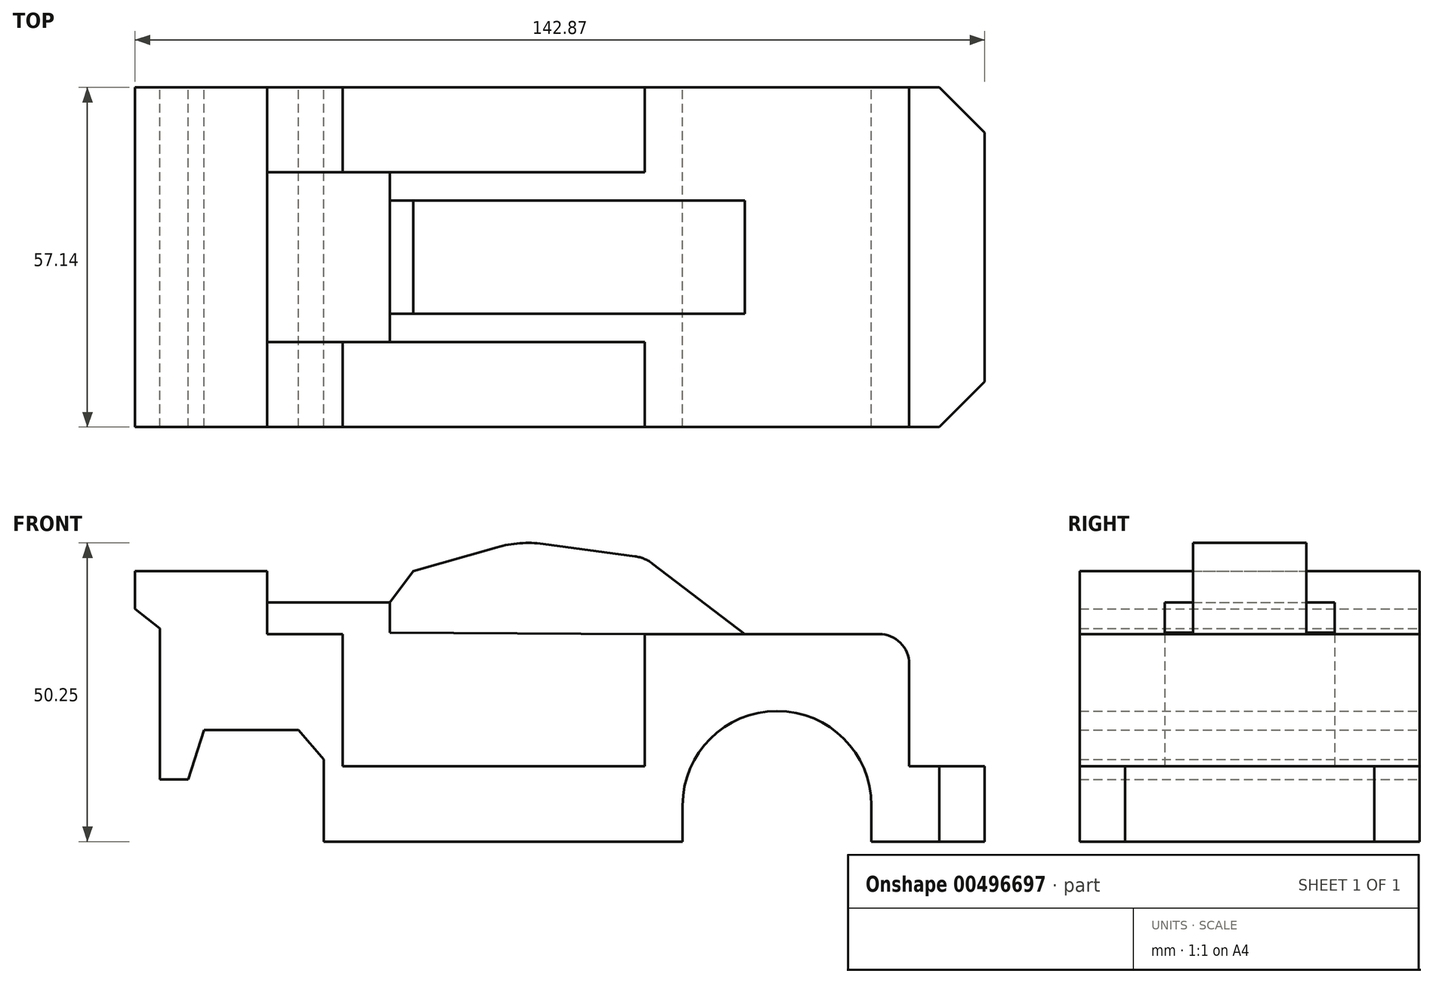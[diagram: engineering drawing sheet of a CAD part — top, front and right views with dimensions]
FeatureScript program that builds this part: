
annotation { "Feature Type Name" : "Feature", "Feature Type Description" : "" }
export const myFeature = defineFeature(function(context is Context, id is Id, definition is map)
    precondition{}
    {
        {
            var Q0;
            Q0=qCreatedBy(makeId("Front.planeOp"),FACE);
            var sketch = newSketch(context, id + "F0", { "sketchPlane" : qUnion([Q0])});
            skLineSegment(sketch, "E0", {"start": v(-32.86, -25.44) * mm, "end": v(27.46, -25.44) * mm});
            skLineSegment(sketch, "E1", {"start": v(-32.86, -25.44) * mm, "end": v(-32.86, -11.64) * mm});
            skLineSegment(sketch, "E2", {"start": v(-55.7, -14.97) * mm, "end": v(-60.47, -14.97) * mm});
            skLineSegment(sketch, "E3", {"start": v(-60.47, -14.97) * mm, "end": v(-60.47, 10.43) * mm});
            skLineSegment(sketch, "E4", {"start": v(-60.47, 10.43) * mm, "end": v(-64.61, 13.74) * mm});
            skLineSegment(sketch, "E5", {"start": v(-64.61, 13.74) * mm, "end": v(-64.61, 20.1) * mm});
            skLineSegment(sketch, "E6", {"start": v(-64.61, 20.1) * mm, "end": v(-42.39, 20.1) * mm});
            skLineSegment(sketch, "E7", {"start": v(-42.39, 20.1) * mm, "end": v(-42.39, 9.48) * mm});
            skLineSegment(sketch, "E8", {"start": v(-42.39, 9.48) * mm, "end": v(-29.69, 9.48) * mm});
            skLineSegment(sketch, "E9", {"start": v(-29.69, 9.48) * mm, "end": v(-29.69, -12.74) * mm});
            skLineSegment(sketch, "E10", {"start": v(-29.69, -12.74) * mm, "end": v(21.11, -12.74) * mm});
            skLineSegment(sketch, "E11", {"start": v(21.11, -12.74) * mm, "end": v(21.11, 9.48) * mm});
            skLineSegment(sketch, "E12", {"start": v(21.11, 9.48) * mm, "end": v(65.56, 9.48) * mm});
            skLineSegment(sketch, "E13", {"start": v(65.56, 9.48) * mm, "end": v(65.56, -12.74) * mm});
            skLineSegment(sketch, "E14", {"start": v(65.56, -12.74) * mm, "end": v(78.26, -12.74) * mm});
            skLineSegment(sketch, "E15", {"start": v(78.26, -12.74) * mm, "end": v(78.26, -18.23) * mm});
            skLineSegment(sketch, "E16", {"start": v(78.26, -18.23) * mm, "end": v(78.26, -25.44) * mm});
            skLineSegment(sketch, "E17", {"start": v(78.26, -25.44) * mm, "end": v(59.21, -25.44) * mm});
            skLineSegment(sketch, "E18", {"start": v(-42.39, 14.79) * mm, "end": v(-21.76, 14.79) * mm});
            skLineSegment(sketch, "E19", {"start": v(-21.76, 14.79) * mm, "end": v(-21.76, 9.7) * mm});
            skLineSegment(sketch, "E20", {"start": v(-21.76, 9.7) * mm, "end": v(-29.69, 9.48) * mm});
            skLineSegment(sketch, "E21", {"start": v(21.11, 9.48) * mm, "end": v(-21.76, 9.7) * mm});
            skLineSegment(sketch, "E22", {"start": v(-21.76, 14.79) * mm, "end": v(-17.81, 20.1) * mm});
            skLineSegment(sketch, "E23", {"start": v(-17.81, 20.1) * mm, "end": v(-3.76, 24.08) * mm});
            skLineSegment(sketch, "E24", {"start": v(3.99, 24.64) * mm, "end": v(19.44, 22.55) * mm});
            skLineSegment(sketch, "E25", {"start": v(22.45, 21.3) * mm, "end": v(37.9, 9.48) * mm});
            skPoint(sketch, "E26.visualSharp", {"position": v(21.11, 22.33) * mm});
            skArc(sketch, "E26.filletArc", {"start": v(22.45, 21.3) * mm, "mid": v(21.03, 22.12) * mm, "end": v(19.44, 22.55) * mm});
            skPoint(sketch, "E27.visualSharp", {"position": v(0.06, 25.17) * mm});
            skArc(sketch, "E27.filletArc", {"start": v(3.99, 24.64) * mm, "mid": v(0.09, 24.76) * mm, "end": v(-3.76, 24.08) * mm});
            skLineSegment(sketch, "E28", {"start": v(-55.7, -14.97) * mm, "end": v(-53.01, -6.67) * mm});
            skLineSegment(sketch, "E29", {"start": v(-53.01, -6.67) * mm, "end": v(-37.14, -6.67) * mm});
            skLineSegment(sketch, "E30", {"start": v(-37.14, -6.67) * mm, "end": v(-32.86, -11.64) * mm});
            skLineSegment(sketch, "E31", {"start": v(27.46, -25.44) * mm, "end": v(27.46, -19.35) * mm});
            skLineSegment(sketch, "E32", {"start": v(59.21, -25.44) * mm, "end": v(59.21, -19.35) * mm});
            skArc(sketch, "E33", {"start": v(59.21, -19.35) * mm, "mid": v(43.34, -3.47) * mm, "end": v(27.46, -19.35) * mm});
            skSolve(sketch);
        }
        {
            var Q0;
            Q0=makeQuery(id+"F0.imprint","IMPRINT",FACE,{"disambiguationData":[TD([[makeQuery(id+"F0.imprint","IMPRINT",EDGE,{"derivedFrom":sQuery(id+"F0.wireOp",EDGE,"E0")}),1.0]])]});
            extrude(context, id + "F1", {"entities" : qUnion([Q0]), "endBound" : BoundingType.SYMMETRIC, "depth" : 57.15 * mm});
        }
        {
            var Q0;
            Q0=makeQuery(id+"F0.imprint","IMPRINT",FACE,{"disambiguationData":[TD([[makeQuery(id+"F0.imprint","IMPRINT",EDGE,{"derivedFrom":sQuery(id+"F0.wireOp",EDGE,"E9")}),1.0]])]});
            extrude(context, id + "F2", {"entities" : qUnion([Q0]), "operationType" : NewBodyOperationType.ADD, "endBound" : BoundingType.SYMMETRIC, "depth" : 28.57 * mm});
        }
        {
            var Q0;
            {var subQ1=sQuery(id+"F0.wireOp",EDGE,"E8");Q0=makeQuery(id+"F0.imprint","IMPRINT",FACE,{"disambiguationData":[TD([[makeQuery(id+"F0.imprint","IMPRINT",EDGE,{"derivedFrom":subQ1}),1.0]])]});}
            extrude(context, id + "F3", {"entities" : qUnion([Q0]), "operationType" : NewBodyOperationType.ADD, "endBound" : BoundingType.SYMMETRIC, "depth" : 28.57 * mm});
        }
        {
            var Q0;
            Q0=makeQuery(id+"F1.opExtrude","SWEPT_EDGE",EDGE,{"disambiguationData":[OSD([sQuery(id+"F0.wireOp",EDGE,"E12"),sQuery(id+"F0.wireOp",EDGE,"E13")])]});
            fillet(context, id + "F4", {"entities" : qUnion([Q0]), "radius" : 5.08 * mm, "tangentPropagation" : true, "allowEdgeOverflow" : false});
        }
        {
            var Q0;
            Q0=makeQuery(id+"F0.imprint","IMPRINT",FACE,{"disambiguationData":[TD([[makeQuery(id+"F0.imprint","IMPRINT",EDGE,{"derivedFrom":sQuery(id+"F0.wireOp",EDGE,"E19")}),1.0]])]});
            extrude(context, id + "F5", {"entities" : qUnion([Q0]), "operationType" : NewBodyOperationType.ADD, "endBound" : BoundingType.SYMMETRIC, "depth" : 19.05 * mm});
        }
        {
            var Q0;
            Q0=makeQuery(id+"F1.opExtrude","CAP_EDGE",EDGE,{"disambiguationData":[OSD([sQuery(id+"F0.wireOp",EDGE,"E15"),sQuery(id+"F0.wireOp",EDGE,"E16")])],"isStart":false});
            var Q1;
            Q1=makeQuery(id+"F1.opExtrude","CAP_EDGE",EDGE,{"disambiguationData":[OSD([sQuery(id+"F0.wireOp",EDGE,"E15"),sQuery(id+"F0.wireOp",EDGE,"E16")])],"isStart":true});
            chamfer(context, id + "F6", {"entities" : qUnion([Q0, Q1]), "width" : 7.62 * mm, "tangentPropagation" : true});
        }
    });
